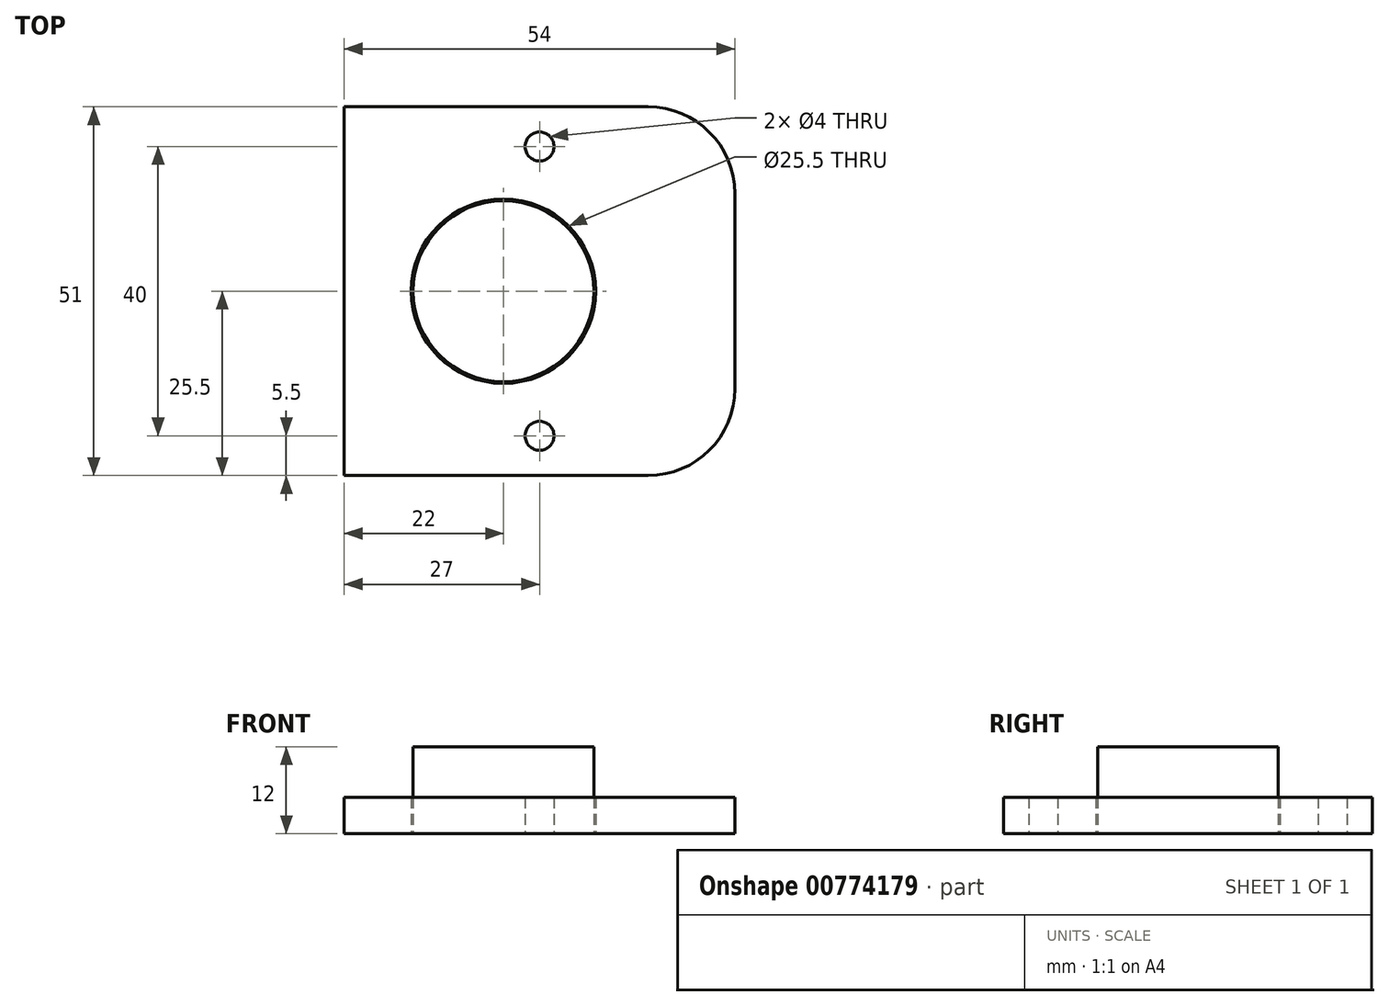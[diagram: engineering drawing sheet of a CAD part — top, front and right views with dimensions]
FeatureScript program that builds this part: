
annotation { "Feature Type Name" : "Feature", "Feature Type Description" : "" }
export const myFeature = defineFeature(function(context is Context, id is Id, definition is map)
    precondition{}
    {
        {
            var Q0;
            Q0=qCreatedBy(makeId("Top.planeOp"),FACE);
            var sketch = newSketch(context, id + "F0", { "sketchPlane" : qUnion([Q0])});
            skLineSegment(sketch, "E0.bottom", {"start": v(27, -25.5) * mm, "end": v(-27, -25.5) * mm});
            skLineSegment(sketch, "E0.top", {"start": v(27, 25.5) * mm, "end": v(-27, 25.5) * mm});
            skLineSegment(sketch, "E0.left", {"start": v(27, -25.5) * mm, "end": v(27, 25.5) * mm});
            skLineSegment(sketch, "E0.right", {"start": v(-27, -25.5) * mm, "end": v(-27, 25.5) * mm});
            skPoint(sketch, "E0.middle", {"position": v(0, 0) * mm});
            skLineSegment(sketch, "E1", {"start": v(0, 0) * mm, "end": v(-5, 0) * mm, "construction": true});
            skCircle(sketch, "E2", {"center": v(-5, 0) * mm, "radius": 12.75 * mm});
            skLineSegment(sketch, "E3", {"start": v(0, 0) * mm, "end": v(0, 20) * mm, "construction": true});
            skLineSegment(sketch, "E4", {"start": v(0, 0) * mm, "end": v(0, -20) * mm, "construction": true});
            skCircle(sketch, "E5", {"center": v(0, 20) * mm, "radius": 2 * mm});
            skCircle(sketch, "E6", {"center": v(0, -20) * mm, "radius": 2 * mm});
            skSolve(sketch);
        }
        {
            var Q0;
            Q0=qSketchRegion(id+"F0",true);
            extrude(context, id + "F1", {"entities" : qUnion([Q0]), "depth" : 5 * mm, "offsetDistance" : 25 * mm});
        }
        {
            var Q0;
            Q0=makeQuery(id+"F1.opExtrude","SWEPT_EDGE",EDGE,{"disambiguationData":[OSD([sQuery(id+"F0.wireOp",EDGE,"E0.bottom"),sQuery(id+"F0.wireOp",EDGE,"E0.left")])]});
            var Q1;
            Q1=makeQuery(id+"F1.opExtrude","SWEPT_EDGE",EDGE,{"disambiguationData":[OSD([sQuery(id+"F0.wireOp",EDGE,"E0.top"),sQuery(id+"F0.wireOp",EDGE,"E0.left")])]});
            fillet(context, id + "F2", {"entities" : qUnion([Q0, Q1]), "radius" : 12 * mm, "tangentPropagation" : true, "allowEdgeOverflow" : false});
        }
        {
            var Q0;
            Q0=qCreatedBy(makeId("Top.planeOp"),FACE);
            var sketch = newSketch(context, id + "F3", { "sketchPlane" : qUnion([Q0])});
            skLineSegment(sketch, "E7", {"start": v(0, 0) * mm, "end": v(-5, 0) * mm});
            skCircle(sketch, "E8", {"center": v(-5, 0) * mm, "radius": 12.5 * mm});
            skSolve(sketch);
        }
        {
            var Q0;
            Q0 = qSketchRegion(id + "F3", true);
            extrude(context, id + "F4", {"entities" : qUnion([Q0]), "depth" : 12 * mm, "offsetDistance" : 25 * mm});
        }
    });
